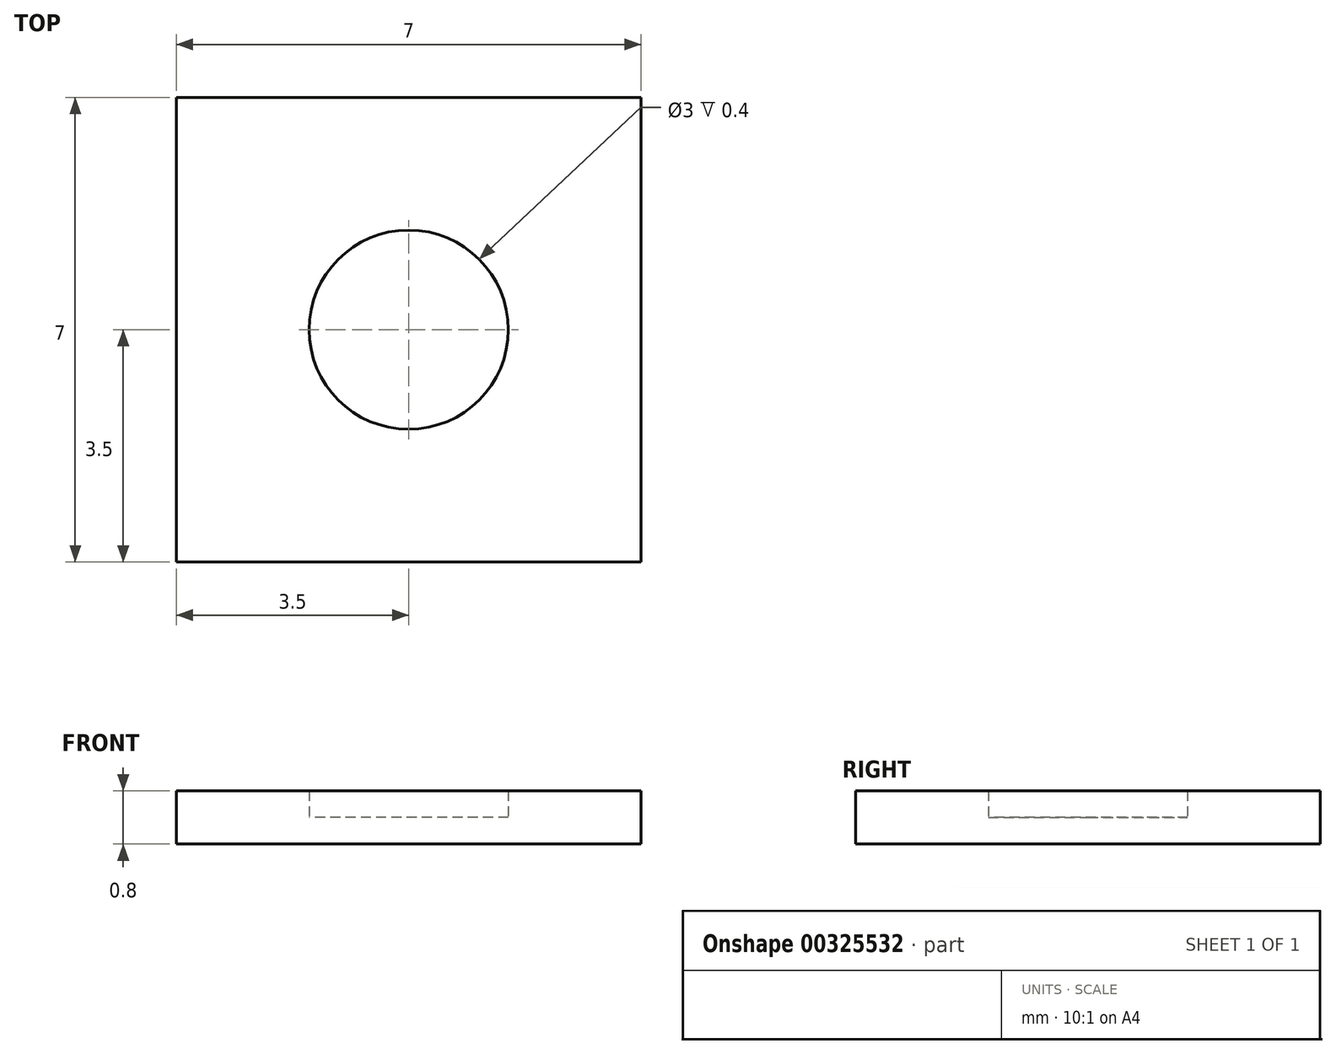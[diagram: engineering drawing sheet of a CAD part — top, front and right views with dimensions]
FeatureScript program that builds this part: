
annotation { "Feature Type Name" : "Feature", "Feature Type Description" : "" }
export const myFeature = defineFeature(function(context is Context, id is Id, definition is map)
    precondition{}
    {
        {
            var Q0;
            Q0=qCreatedBy(makeId("Top.planeOp"),FACE);
            var sketch = newSketch(context, id + "F0", { "sketchPlane" : qUnion([Q0])});
            skLineSegment(sketch, "E0.bottom", {"start": v(3.5, -3.5) * mm, "end": v(-3.5, -3.5) * mm});
            skLineSegment(sketch, "E0.top", {"start": v(3.5, 3.5) * mm, "end": v(-3.5, 3.5) * mm});
            skLineSegment(sketch, "E0.left", {"start": v(3.5, -3.5) * mm, "end": v(3.5, 3.5) * mm});
            skLineSegment(sketch, "E0.right", {"start": v(-3.5, -3.5) * mm, "end": v(-3.5, 3.5) * mm});
            skPoint(sketch, "E0.middle", {"position": v(0, 0) * mm});
            skCircle(sketch, "E1", {"center": v(0, 0) * mm, "radius": 1.5 * mm});
            skSolve(sketch);
        }
        {
            var Q0;
            Q0=makeQuery(id+"F0.imprint","IMPRINT",FACE,{"disambiguationData":[TD([[makeQuery(id+"F0.imprint","IMPRINT",EDGE,{"derivedFrom":sQuery(id+"F0.wireOp",EDGE,"E1")}),1.0]])]});
            extrude(context, id + "F1", {"entities" : qUnion([Q0]), "depth" : 0.4 * mm});
        }
        {
            var Q0;
            Q0 = qSketchRegion(id + "F0", true);
            extrude(context, id + "F2", {"entities" : qUnion([Q0]), "operationType" : NewBodyOperationType.ADD, "depth" : 0.8 * mm});
        }
    });
